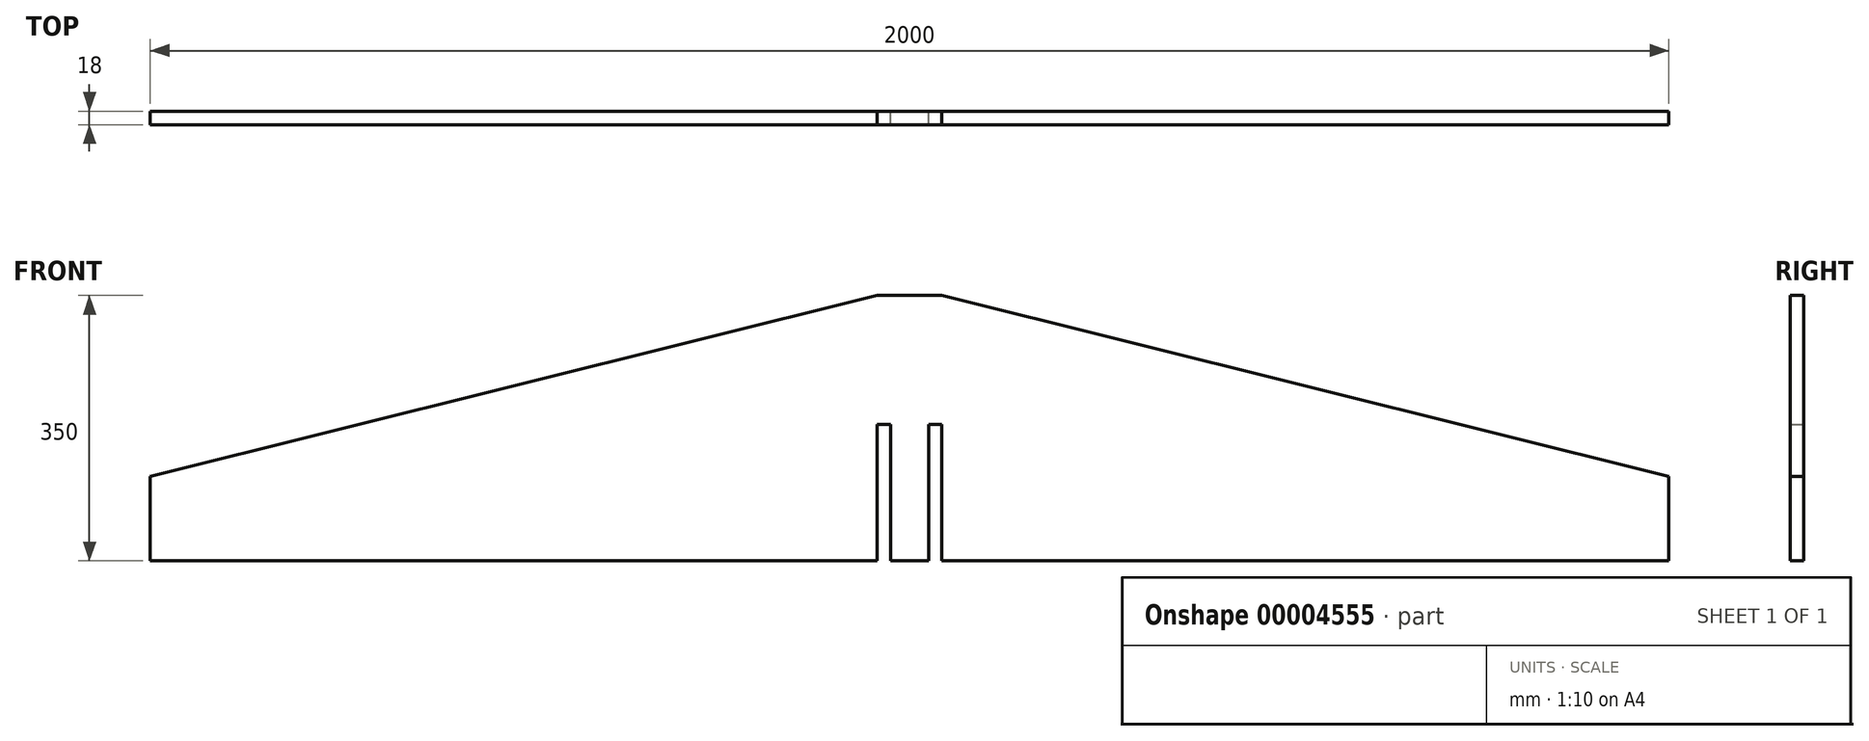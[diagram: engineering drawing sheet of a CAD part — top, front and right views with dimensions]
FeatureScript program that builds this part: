
annotation { "Feature Type Name" : "Feature", "Feature Type Description" : "" }
export const myFeature = defineFeature(function(context is Context, id is Id, definition is map)
    precondition{}
    {
        {
            var Q0;
            Q0=qCreatedBy(makeId("Front.planeOp"),FACE);
            var sketch = newSketch(context, id + "F0", { "sketchPlane" : qUnion([Q0])});
            skLineSegment(sketch, "E0", {"start": v(355.7, 350.59) * mm, "end": v(355.7, -41.28) * mm, "construction": true});
            skLineSegment(sketch, "E1", {"start": v(355.7, -41.28) * mm, "end": v(380.7, -41.28) * mm});
            skLineSegment(sketch, "E2", {"start": v(1355.7, -41.28) * mm, "end": v(1355.7, 69.96) * mm});
            skLineSegment(sketch, "E3", {"start": v(1355.7, 69.96) * mm, "end": v(398.4, 308.72) * mm});
            skLineSegment(sketch, "E4.0.MirrorCS", {"start": v(-644.3, 69.96) * mm, "end": v(313, 308.72) * mm});
            skLineSegment(sketch, "E5.0.MirrorCS", {"start": v(-644.3, -41.28) * mm, "end": v(-644.3, 69.96) * mm});
            skLineSegment(sketch, "E6.0.MirrorCS", {"start": v(355.7, -41.28) * mm, "end": v(330.7, -41.28) * mm});
            skLineSegment(sketch, "E7.0.MirrorCS", {"start": v(313, 138.72) * mm, "end": v(313, -41.28) * mm});
            skLineSegment(sketch, "E8", {"start": v(330.7, 138.72) * mm, "end": v(330.7, -41.28) * mm});
            skLineSegment(sketch, "E9.0.MirrorCS", {"start": v(380.7, 138.72) * mm, "end": v(380.7, -41.28) * mm});
            skLineSegment(sketch, "E9.1.MirrorCS", {"start": v(398.4, 138.72) * mm, "end": v(398.4, -41.28) * mm});
            skLineSegment(sketch, "E10.trimOffspring", {"start": v(313, -41.28) * mm, "end": v(-644.3, -41.28) * mm});
            skLineSegment(sketch, "E11.trimOffspring", {"start": v(398.4, -41.28) * mm, "end": v(1355.7, -41.28) * mm});
            skLineSegment(sketch, "E12", {"start": v(313, 138.72) * mm, "end": v(330.7, 138.72) * mm});
            skPoint(sketch, "E13.orphan", {"position": v(313, 308.72) * mm});
            skLineSegment(sketch, "E14", {"start": v(313, 308.72) * mm, "end": v(398.4, 308.72) * mm});
            skLineSegment(sketch, "E15.trimOffspring", {"start": v(380.7, 138.72) * mm, "end": v(398.4, 138.72) * mm});
            skSolve(sketch);
        }
        {
            var Q0;
            Q0=qSketchRegion(id+"F0",true);
            extrude(context, id + "F1", {"entities" : qUnion([Q0]), "depth" : 18 * mm});
        }
        {
            var Q0;
            Q0=qCreatedBy(makeId("Front.planeOp"),FACE);
            var sketch = newSketch(context, id + "F2", { "sketchPlane" : qUnion([Q0])});
            skLineSegment(sketch, "E16", {"start": v(1876.04, 0) * mm, "end": v(2866.04, 0) * mm});
            skLineSegment(sketch, "E17", {"start": v(2866.04, 0) * mm, "end": v(2866.04, 110.73) * mm});
            skLineSegment(sketch, "E18", {"start": v(2866.04, 110.73) * mm, "end": v(1866.04, 350) * mm});
            skLineSegment(sketch, "E19", {"start": v(1866.04, 350) * mm, "end": v(1866.04, 0) * mm, "construction": true});
            skLineSegment(sketch, "E20", {"start": v(1866.04, 175) * mm, "end": v(1876.04, 175) * mm});
            skLineSegment(sketch, "E21", {"start": v(1876.04, 175) * mm, "end": v(1876.04, 0) * mm});
            skLineSegment(sketch, "E22.0.MirrorCS", {"start": v(866.04, 110.73) * mm, "end": v(1866.04, 350) * mm});
            skLineSegment(sketch, "E23.0.MirrorCS", {"start": v(866.04, 0) * mm, "end": v(866.04, 110.73) * mm});
            skLineSegment(sketch, "E24.0.MirrorCS", {"start": v(1856.04, 0) * mm, "end": v(866.04, 0) * mm});
            skLineSegment(sketch, "E25.0.MirrorCS", {"start": v(1856.04, 175) * mm, "end": v(1856.04, 0) * mm});
            skLineSegment(sketch, "E26.0.MirrorCS", {"start": v(1866.04, 175) * mm, "end": v(1856.04, 175) * mm});
            skSolve(sketch);
        }
        {
            var Q0;
            Q0=qSketchRegion(id+"F2",true);
            extrude(context, id + "F3", {"entities" : qUnion([Q0]), "depth" : 18 * mm});
        }
        {
            var Q0;
            Q0=makeQuery(id+"F3.opExtrude","SWEPT_BODY",BODY,{"disambiguationData":[OSD([sQuery(id+"F2.wireOp",EDGE,"E16"),sQuery(id+"F2.wireOp",EDGE,"E17"),sQuery(id+"F2.wireOp",EDGE,"E18"),sQuery(id+"F2.wireOp",EDGE,"E21"),sQuery(id+"F2.wireOp",EDGE,"E22.0.MirrorCS"),sQuery(id+"F2.wireOp",EDGE,"E23.0.MirrorCS"),sQuery(id+"F2.wireOp",EDGE,"E24.0.MirrorCS"),sQuery(id+"F2.wireOp",EDGE,"E25.0.MirrorCS"),sQuery(id+"F2.wireOp",EDGE,"E26.0.MirrorCS")])]});
            deleteBodies(context, id + "F4", {"entities" : qUnion([Q0])});
        }
    });
